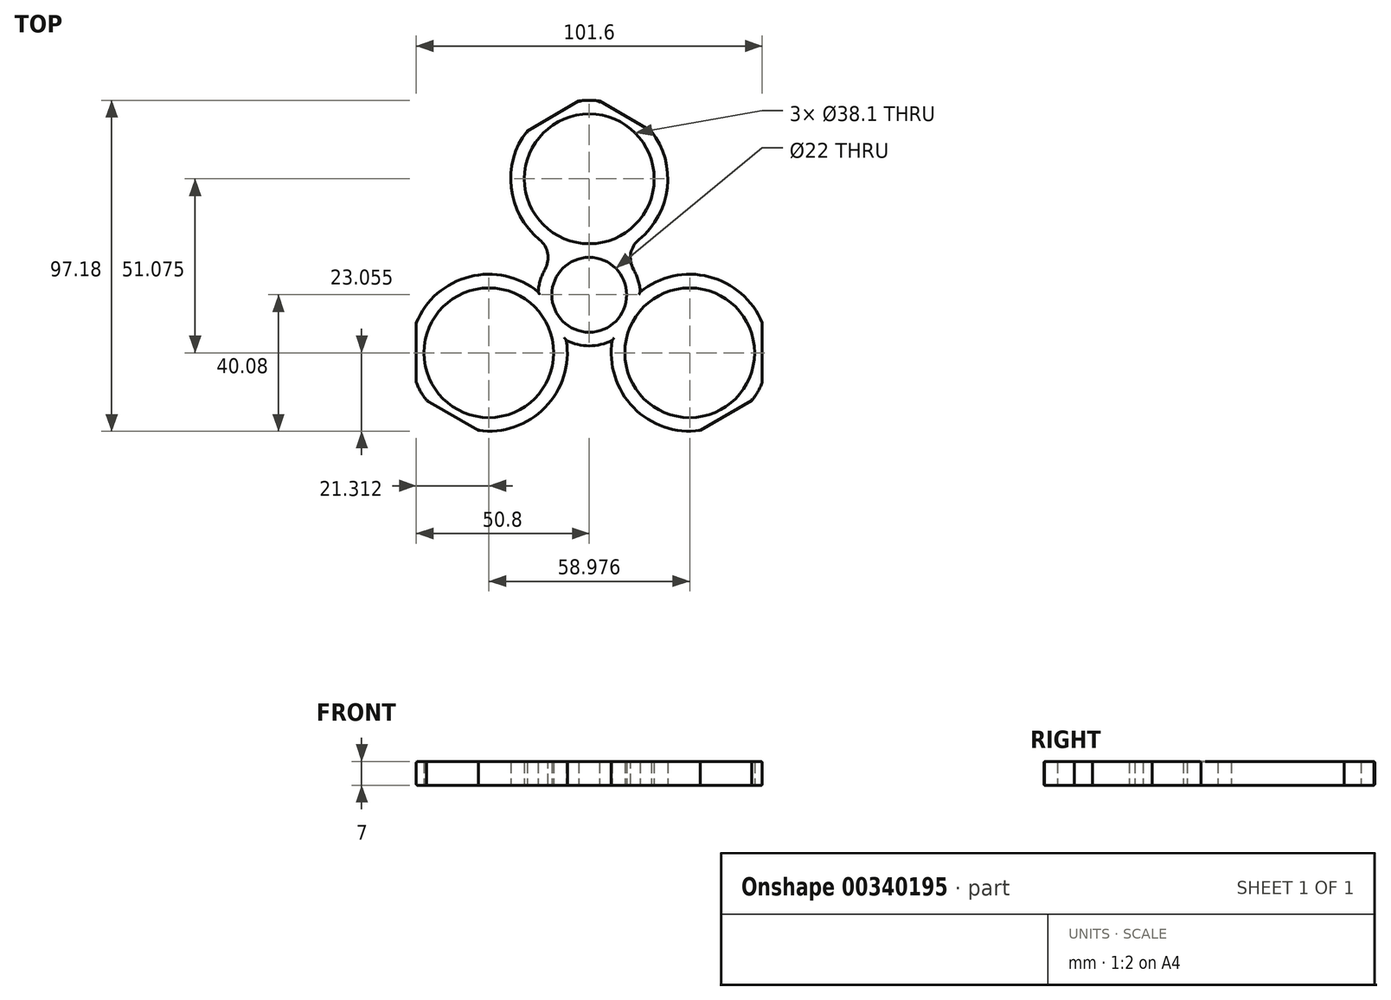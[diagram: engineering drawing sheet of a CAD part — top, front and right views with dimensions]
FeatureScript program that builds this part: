
annotation { "Feature Type Name" : "Feature", "Feature Type Description" : "" }
export const myFeature = defineFeature(function(context is Context, id is Id, definition is map)
    precondition{}
    {
        {
            var Q0;
            Q0=qCreatedBy(makeId("Top.planeOp"),FACE);
            var sketch = newSketch(context, id + "F0", { "sketchPlane" : qUnion([Q0])});
            skCircle(sketch, "E0", {"center": v(0, 34.05) * mm, "radius": 19.05 * mm});
            skCircle(sketch, "E1", {"center": v(0, 0) * mm, "radius": 11 * mm});
            skLineSegment(sketch, "E2", {"start": v(0, 0) * mm, "end": v(0, 15) * mm});
            skArc(sketch, "E3", {"start": v(8.25, 12.53) * mm, "mid": v(0, 57.1) * mm, "end": v(-8.25, 12.53) * mm});
            skArc(sketch, "E4", {"start": v(-8.25, 12.53) * mm, "mid": v(0, -15) * mm, "end": v(8.25, 12.53) * mm});
            skSolve(sketch);
        }
        {
            var Q0;
            Q0=makeQuery(id+"F0.imprint","IMPRINT",FACE,{"disambiguationData":[TD([[makeQuery(id+"F0.imprint","IMPRINT",EDGE,{"derivedFrom":sQuery(id+"F0.wireOp",EDGE,"E0")}),-1.0]])]});
            extrude(context, id + "F1", {"entities" : qUnion([Q0]), "depth" : 7 * mm});
        }
        {
            var Q0;
            Q0=makeQuery(id+"F1.opExtrude","SWEPT_BODY",BODY,{"disambiguationData":[OSD([sQuery(id+"F0.wireOp",EDGE,"E0"),sQuery(id+"F0.wireOp",EDGE,"E1"),sQuery(id+"F0.wireOp",EDGE,"E3"),sQuery(id+"F0.wireOp",EDGE,"E4")])]});
            var Q1;
            Q1=makeQuery(id+"F1.opExtrude","CAP_EDGE",EDGE,{"disambiguationData":[OSD([sQuery(id+"F0.wireOp",EDGE,"E1")])],"isStart":false});
            circularPattern(context, id + "F2", {"operationType" : NewBodyOperationType.ADD, "entities" : qUnion([Q0]), "axis" : qUnion([Q1]), "angle" : 360 * degree, "instanceCount" : 3, "equalSpace" : true});
        }
        {
            var Q0;
            {var subQ0=sQuery(id+"F0.wireOp",EDGE,"E4");var subQ1=sQuery(id+"F0.wireOp",EDGE,"E3");Q0=makeQuery(id+"F1.opExtrude","SWEPT_EDGE",EDGE,{"disambiguationData":[OSD([subQ1,subQ0]),TDD([makeQuery(id+"F0.imprint","INTERSECT",VERTEX,{"disambiguationData":[OD(0.0)],"derivedFrom":[subQ1,subQ0]})])]});}
            var Q1;
            {var subQ0=sQuery(id+"F0.wireOp",EDGE,"E4");var subQ1=sQuery(id+"F0.wireOp",EDGE,"E3");Q1=makeQuery(id+"F2.opPattern","COPY",EDGE,{"derivedFrom":makeQuery(id+"F1.opExtrude","SWEPT_EDGE",EDGE,{"disambiguationData":[OSD([subQ1,subQ0]),TDD([makeQuery(id+"F0.imprint","INTERSECT",VERTEX,{"disambiguationData":[OD(1.0)],"derivedFrom":[subQ1,subQ0]})])]}),"instanceName":"2"});}
            var Q2;
            {var subQ0=sQuery(id+"F0.wireOp",EDGE,"E4");var subQ1=sQuery(id+"F0.wireOp",EDGE,"E3");Q2=makeQuery(id+"F2.opPattern","COPY",EDGE,{"derivedFrom":makeQuery(id+"F1.opExtrude","SWEPT_EDGE",EDGE,{"disambiguationData":[OSD([subQ1,subQ0]),TDD([makeQuery(id+"F0.imprint","INTERSECT",VERTEX,{"disambiguationData":[OD(0.0)],"derivedFrom":[subQ1,subQ0]})])]}),"instanceName":"2"});}
            var Q3;
            {var subQ0=sQuery(id+"F0.wireOp",EDGE,"E4");var subQ1=sQuery(id+"F0.wireOp",EDGE,"E3");Q3=makeQuery(id+"F2.opPattern","COPY",EDGE,{"derivedFrom":makeQuery(id+"F1.opExtrude","SWEPT_EDGE",EDGE,{"disambiguationData":[OSD([subQ1,subQ0]),TDD([makeQuery(id+"F0.imprint","INTERSECT",VERTEX,{"disambiguationData":[OD(1.0)],"derivedFrom":[subQ1,subQ0]})])]}),"instanceName":"1"});}
            var Q4;
            {var subQ0=sQuery(id+"F0.wireOp",EDGE,"E4");var subQ1=sQuery(id+"F0.wireOp",EDGE,"E3");Q4=makeQuery(id+"F1.opExtrude","SWEPT_EDGE",EDGE,{"disambiguationData":[OSD([subQ1,subQ0]),TDD([makeQuery(id+"F0.imprint","INTERSECT",VERTEX,{"disambiguationData":[OD(1.0)],"derivedFrom":[subQ1,subQ0]})])]});}
            var Q5;
            {var subQ0=sQuery(id+"F0.wireOp",EDGE,"E4");var subQ1=sQuery(id+"F0.wireOp",EDGE,"E3");Q5=makeQuery(id+"F2.opPattern","COPY",EDGE,{"derivedFrom":makeQuery(id+"F1.opExtrude","SWEPT_EDGE",EDGE,{"disambiguationData":[OSD([subQ1,subQ0]),TDD([makeQuery(id+"F0.imprint","INTERSECT",VERTEX,{"disambiguationData":[OD(0.0)],"derivedFrom":[subQ1,subQ0]})])]}),"instanceName":"1"});}
            fillet(context, id + "F3", {"entities" : qUnion([Q0, Q1, Q2, Q3, Q4, Q5]), "radius" : 6.86 * mm, "tangentPropagation" : true, "allowEdgeOverflow" : false});
        }
        {
            var Q0;
            Q0=qCreatedBy(makeId("Top.planeOp"),FACE);
            var sketch = newSketch(context, id + "F4", { "sketchPlane" : qUnion([Q0])});
            skCircle(sketch, "E5.cCircle", {"center": v(0, 0) * mm, "radius": 50.8 * mm, "construction": true});
            skLineSegment(sketch, "E5.0", {"start": v(50.8, 29.33) * mm, "end": v(50.8, -29.33) * mm});
            skLineSegment(sketch, "E5.1", {"start": v(50.8, -29.33) * mm, "end": v(0, -58.66) * mm});
            skLineSegment(sketch, "E5.2", {"start": v(0, -58.66) * mm, "end": v(-50.8, -29.33) * mm});
            skLineSegment(sketch, "E5.3", {"start": v(-50.8, -29.33) * mm, "end": v(-50.8, 29.33) * mm});
            skLineSegment(sketch, "E5.4", {"start": v(-50.8, 29.33) * mm, "end": v(0, 58.66) * mm});
            skLineSegment(sketch, "E5.5", {"start": v(0, 58.66) * mm, "end": v(50.8, 29.33) * mm});
            skPoint(sketch, "E5.0.midPoint", {"position": v(50.8, 0) * mm});
            skCircle(sketch, "E6.cCircle", {"center": v(0, 0) * mm, "radius": 68.07 * mm, "construction": true});
            skLineSegment(sketch, "E6.0", {"start": v(68.07, 39.3) * mm, "end": v(68.07, -39.3) * mm});
            skLineSegment(sketch, "E6.1", {"start": v(68.07, -39.3) * mm, "end": v(0, -78.6) * mm});
            skLineSegment(sketch, "E6.2", {"start": v(0, -78.6) * mm, "end": v(-68.07, -39.3) * mm});
            skLineSegment(sketch, "E6.3", {"start": v(-68.07, -39.3) * mm, "end": v(-68.07, 39.3) * mm});
            skLineSegment(sketch, "E6.4", {"start": v(-68.07, 39.3) * mm, "end": v(0, 78.6) * mm});
            skLineSegment(sketch, "E6.5", {"start": v(0, 78.6) * mm, "end": v(68.07, 39.3) * mm});
            skPoint(sketch, "E6.0.midPoint", {"position": v(68.07, 0) * mm});
            skSolve(sketch);
        }
        {
            var Q0;
            Q0=makeQuery(id+"F4.imprint","IMPRINT",FACE,{"disambiguationData":[TD([[makeQuery(id+"F4.imprint","IMPRINT",EDGE,{"derivedFrom":sQuery(id+"F4.wireOp",EDGE,"E5.0")}),1.0]])]});
            extrude(context, id + "F5", {"entities" : qUnion([Q0]), "operationType" : NewBodyOperationType.REMOVE, "depth" : 25.4 * mm});
        }
        {
            var Q0;
            {var subQ0=makeQuery(id+"F1.opExtrude","CAP_FACE",FACE,{"disambiguationData":[OSD([sQuery(id+"F0.wireOp",EDGE,"E0"),sQuery(id+"F0.wireOp",EDGE,"E1"),sQuery(id+"F0.wireOp",EDGE,"E3"),sQuery(id+"F0.wireOp",EDGE,"E4")])],"isStart":false});Q0=makeQuery(id+"F2.boolean.opBoolean","MERGE",FACE,{"derivedFrom":[subQ0,makeQuery(id+"F2.opPattern","COPY",FACE,{"derivedFrom":subQ0,"instanceName":"1"}),makeQuery(id+"F2.opPattern","COPY",FACE,{"derivedFrom":subQ0,"instanceName":"2"})]});}
            var Q1;
            {var subQ0=makeQuery(id+"F1.opExtrude","CAP_FACE",FACE,{"disambiguationData":[OSD([sQuery(id+"F0.wireOp",EDGE,"E0"),sQuery(id+"F0.wireOp",EDGE,"E1"),sQuery(id+"F0.wireOp",EDGE,"E3"),sQuery(id+"F0.wireOp",EDGE,"E4")])],"isStart":true});Q1=makeQuery(id+"F2.boolean.opBoolean","MERGE",FACE,{"derivedFrom":[subQ0,makeQuery(id+"F2.opPattern","COPY",FACE,{"derivedFrom":subQ0,"instanceName":"1"}),makeQuery(id+"F2.opPattern","COPY",FACE,{"derivedFrom":subQ0,"instanceName":"2"})]});}
            fillet(context, id + "F6", {"entities" : qUnion([Q0, Q1]), "radius" : 0.4 * mm, "tangentPropagation" : true, "allowEdgeOverflow" : false});
        }
    });
